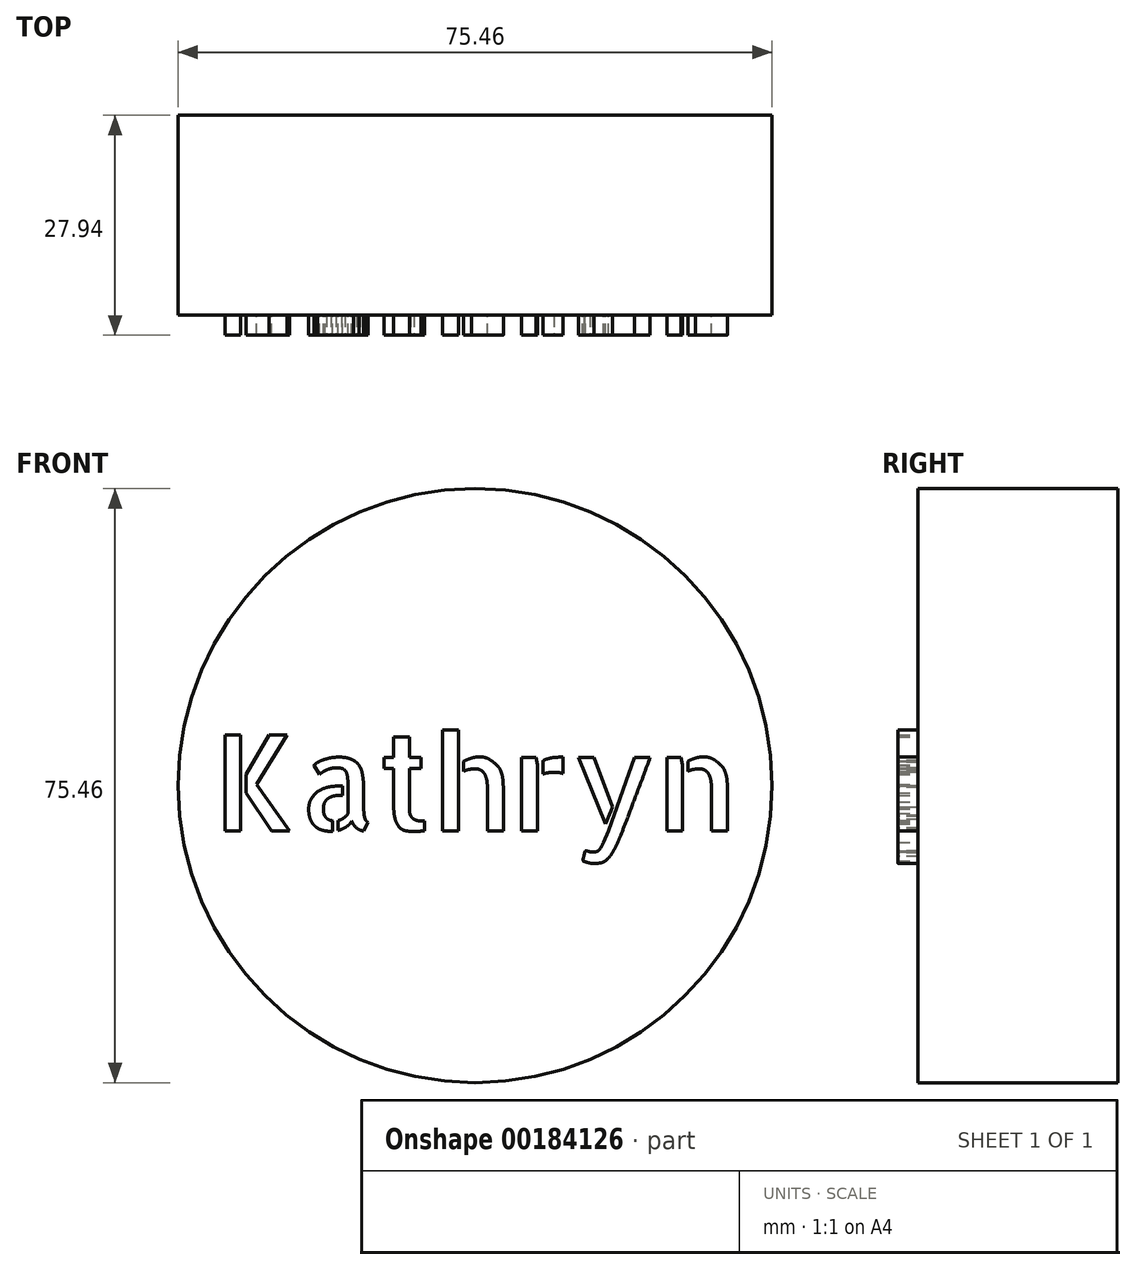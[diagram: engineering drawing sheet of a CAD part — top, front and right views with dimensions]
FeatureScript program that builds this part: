
annotation { "Feature Type Name" : "Feature", "Feature Type Description" : "" }
export const myFeature = defineFeature(function(context is Context, id is Id, definition is map)
    precondition{}
    {
        {
            var Q0;
            Q0=qCreatedBy(makeId("Front.planeOp"),FACE);
            var sketch = newSketch(context, id + "F0", { "sketchPlane" : qUnion([Q0])});
            skCircle(sketch, "E0", {"center": v(0, 0) * mm, "radius": 37.73 * mm});
            skSolve(sketch);
        }
        {
            var Q0;
            Q0=qCreatedBy(makeId("Front.planeOp"),FACE);
            var sketch = newSketch(context, id + "F1", { "sketchPlane" : qUnion([Q0])});
            skText(sketch, "E1", { "text": "Kathryn", "fontName": "AllertaStencil-Regular.ttf"});
            const initialGuessF1  = {"E1": [-0.03332, -0.00573, 1, 0, 0.01215]};
            skSetInitialGuess(sketch, initialGuessF1);
            skSolve(sketch);
        }
        {
            var Q0;
            Q0=makeQuery(id+"F0.imprint","IMPRINT",FACE,{"disambiguationData":[TD([[makeQuery(id+"F0.imprint","IMPRINT",EDGE,{"derivedFrom":sQuery(id+"F0.wireOp",EDGE,"E0")}),1.0]])]});
            extrude(context, id + "F2", {"entities" : qUnion([Q0]), "oppositeDirection" : true, "depth" : 25.4 * mm});
        }
        {
            var Q0;
            Q0 = qSketchRegion(id + "F1", true);
            extrude(context, id + "F3", {"entities" : qUnion([Q0]), "operationType" : NewBodyOperationType.ADD, "depth" : 2.54 * mm});
        }
    });
